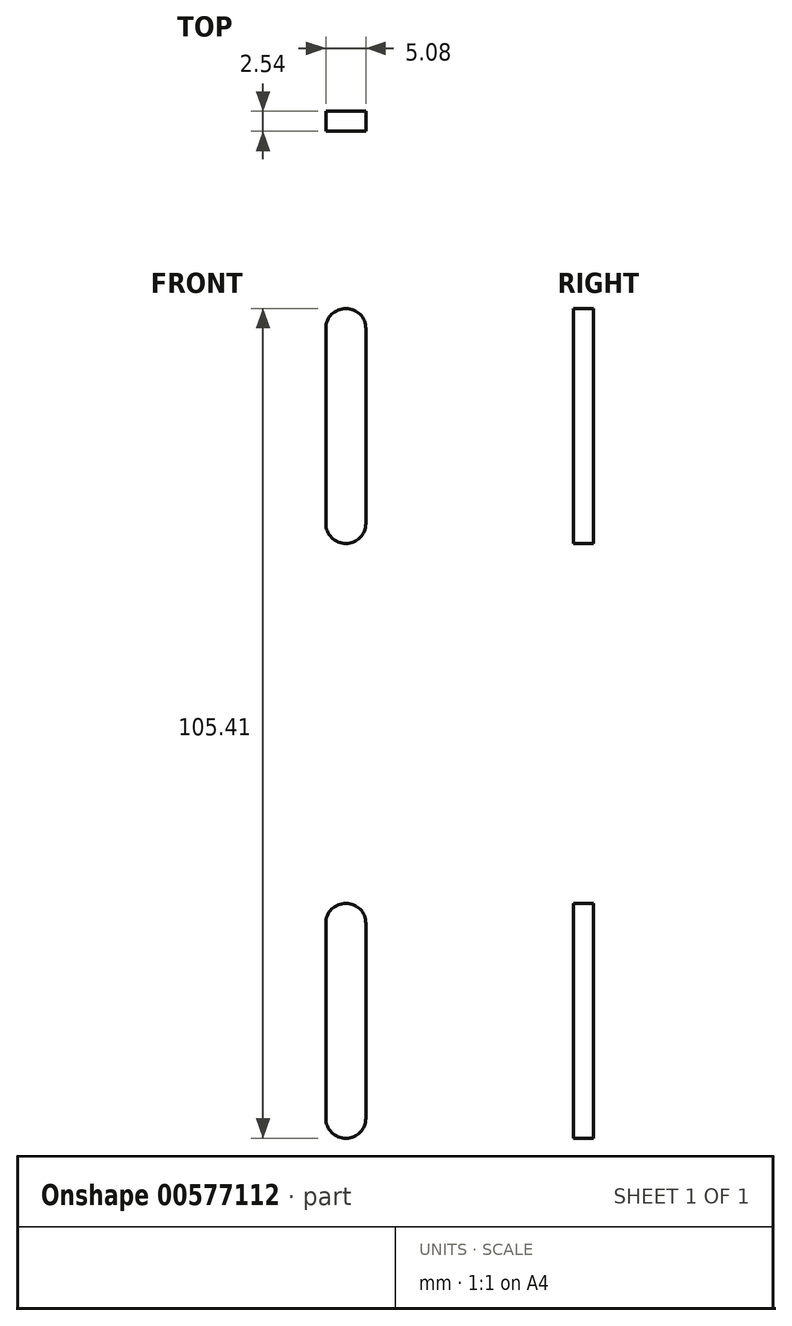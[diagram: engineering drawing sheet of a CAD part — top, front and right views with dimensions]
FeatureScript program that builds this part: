
annotation { "Feature Type Name" : "Feature", "Feature Type Description" : "" }
export const myFeature = defineFeature(function(context is Context, id is Id, definition is map)
    precondition{}
    {
        {
            var Q0;
            Q0=qCreatedBy(makeId("Front.planeOp"),FACE);
            var sketch = newSketch(context, id + "F0", { "sketchPlane" : qUnion([Q0])});
            skLineSegment(sketch, "E0.bottom", {"start": v(3.81, 0) * mm, "end": v(15.24, 0) * mm});
            skLineSegment(sketch, "E0.top", {"start": v(3.8, 120.65) * mm, "end": v(15.24, 120.65) * mm});
            skLineSegment(sketch, "E0.left", {"start": v(0, 3.81) * mm, "end": v(0, 116.84) * mm});
            skLineSegment(sketch, "E0.right", {"start": v(19.05, 3.81) * mm, "end": v(19.05, 116.84) * mm});
            skPoint(sketch, "E1.visualSharp", {"position": v(0, 120.65) * mm});
            skArc(sketch, "E1.filletArc", {"start": v(3.8, 120.65) * mm, "mid": v(1.12, 119.53) * mm, "end": v(0, 116.84) * mm});
            skPoint(sketch, "E2.visualSharp", {"position": v(19.05, 120.65) * mm});
            skArc(sketch, "E2.filletArc", {"start": v(19.05, 116.84) * mm, "mid": v(17.93, 119.53) * mm, "end": v(15.24, 120.65) * mm});
            skPoint(sketch, "E3.visualSharp", {"position": v(19.05, 0) * mm});
            skArc(sketch, "E3.filletArc", {"start": v(15.24, 0) * mm, "mid": v(17.93, 1.12) * mm, "end": v(19.05, 3.81) * mm});
            skPoint(sketch, "E4.visualSharp", {"position": v(0, 0) * mm});
            skArc(sketch, "E4.filletArc", {"start": v(0, 3.8) * mm, "mid": v(1.12, 1.12) * mm, "end": v(3.81, 0) * mm});
            skSolve(sketch);
        }
        {
            var Q0;
            Q0 = qSketchRegion(id + "F0", true);
            extrude(context, id + "F1", {"entities" : qUnion([Q0]), "depth" : 2.54 * mm, "offsetDistance" : 25.4 * mm});
        }
        {
            var Q0;
            Q0=makeQuery(id+"F1.opExtrude","CAP_FACE",FACE,{"disambiguationData":[OSD([sQuery(id+"F0.wireOp",EDGE,"E0.bottom"),sQuery(id+"F0.wireOp",EDGE,"E0.top"),sQuery(id+"F0.wireOp",EDGE,"E0.left"),sQuery(id+"F0.wireOp",EDGE,"E0.right"),sQuery(id+"F0.wireOp",EDGE,"E1.filletArc"),sQuery(id+"F0.wireOp",EDGE,"E2.filletArc"),sQuery(id+"F0.wireOp",EDGE,"E3.filletArc"),sQuery(id+"F0.wireOp",EDGE,"E4.filletArc")])],"isStart":false});
            var sketch = newSketch(context, id + "F2", { "sketchPlane" : qUnion([Q0])});
            skLineSegment(sketch, "E5", {"start": v(9.52, 110.5) * mm, "end": v(9.52, 85.73) * mm});
            skLineSegment(sketch, "E6", {"start": v(0, 110.5) * mm, "end": v(19.05, 110.5) * mm, "construction": true});
            skLineSegment(sketch, "E7", {"start": v(19.05, 10.16) * mm, "end": v(0, 10.16) * mm, "construction": true});
            skLineSegment(sketch, "E8", {"start": v(9.52, 10.16) * mm, "end": v(9.52, 34.92) * mm});
            skArc(sketch, "E9.0.startCap", {"start": v(6.98, 110.5) * mm, "mid": v(9.52, 113.03) * mm, "end": v(12.06, 110.5) * mm});
            skArc(sketch, "E9.0.endCap", {"start": v(12.06, 85.73) * mm, "mid": v(9.52, 83.19) * mm, "end": v(6.98, 85.73) * mm});
            skLineSegment(sketch, "E9.0.left", {"start": v(12.06, 110.5) * mm, "end": v(12.06, 85.73) * mm});
            skLineSegment(sketch, "E9.0.right", {"start": v(6.98, 110.5) * mm, "end": v(6.98, 85.73) * mm});
            skArc(sketch, "E10.0.startCap", {"start": v(12.06, 10.16) * mm, "mid": v(9.52, 7.62) * mm, "end": v(6.98, 10.16) * mm});
            skArc(sketch, "E10.0.endCap", {"start": v(6.98, 34.92) * mm, "mid": v(9.52, 37.46) * mm, "end": v(12.06, 34.92) * mm});
            skLineSegment(sketch, "E10.0.left", {"start": v(6.98, 10.16) * mm, "end": v(6.98, 34.92) * mm});
            skLineSegment(sketch, "E10.0.right", {"start": v(12.06, 10.16) * mm, "end": v(12.06, 34.92) * mm});
            skSolve(sketch);
        }
        {
            var Q0;
            Q0=makeQuery(id+"F2.imprint","IMPRINT",FACE,{"disambiguationData":[TD([[makeQuery(id+"F2.imprint","IMPRINT",EDGE,{"derivedFrom":sQuery(id+"F2.wireOp",EDGE,"E9.0.startCap")}),-1.0]])]});
            var Q1;
            Q1=makeQuery(id+"F2.imprint","IMPRINT",FACE,{"disambiguationData":[TD([[makeQuery(id+"F2.imprint","IMPRINT",EDGE,{"derivedFrom":sQuery(id+"F2.wireOp",EDGE,"E10.0.startCap")}),-1.0]])]});
            extrude(context, id + "F3", {"entities" : qUnion([Q0, Q1]), "operationType" : NewBodyOperationType.REMOVE, "endBound" : BoundingType.THROUGH_ALL, "oppositeDirection" : true, "depth" : 25.4 * mm, "offsetDistance" : 25.4 * mm});
        }
    });
